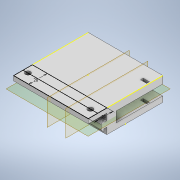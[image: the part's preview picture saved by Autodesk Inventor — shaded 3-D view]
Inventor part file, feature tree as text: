
AUTODESK INVENTOR PART (.ipt)
format: ipt  version: 2022 (Build 260153000, 153)  size: 182,784 bytes
history: native  units: mm
features: sketch x17, other x4, extrude x4, hole x1
ambient origin geometry x8: Origin, YZ Plane, XZ Plane, XY Plane, X Axis, Y Axis, Z Axis, Center Point
bodies: Body1 (feature_tree)
feature tree (26):
  other  "솔리드1"
  sketch  "스케치1"
  extrude  "돌출1"  Depth=80.0mm
  sketch  "스케치3"
  other  "작업 평면1"
  sketch  "스케치4"
  sketch  "스케치5"
  sketch  "스케치6"
  sketch  "스케치7"
  sketch  "스케치8"
  other  "작업 평면2"
  extrude  "돌출2"  Depth=80.0mm
  other  "작업 평면3"
  sketch  "스케치10"
  sketch  "스케치11"
  extrude  "돌출3"  Depth=25.0mm TaperAngle=0.0deg
  sketch  "스케치14"
  sketch  "스케치15"
  hole  "구멍2"  [1 undecoded]
  sketch  "스케치17"
  sketch  "스케치19"
  extrude  "돌출5"  Depth=20.0mm
  sketch  "스케치2"
  sketch  "스케치12"
  sketch  "스케치16"
  sketch  "스케치20"
note: 1 required parameter value undecoded (feature->parameter linkage not recoverable at this tier; creation-order binding heuristic only, values carry confidence <= 0.55)
